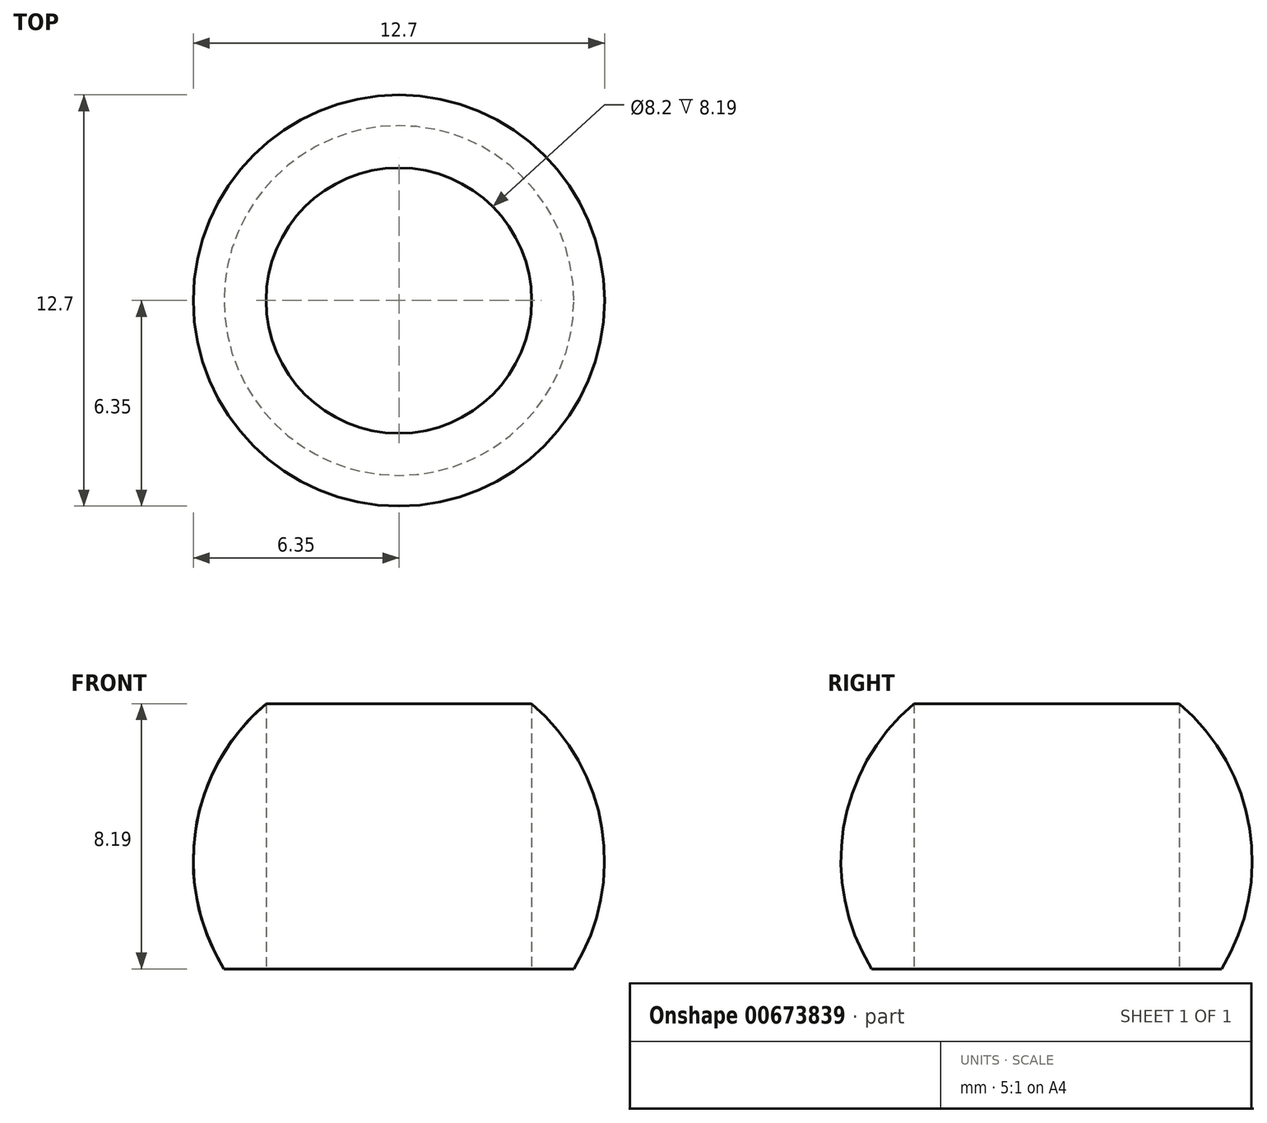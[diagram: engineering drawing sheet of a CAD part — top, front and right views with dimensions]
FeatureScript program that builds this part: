
annotation { "Feature Type Name" : "Feature", "Feature Type Description" : "" }
export const myFeature = defineFeature(function(context is Context, id is Id, definition is map)
    precondition{}
    {
        {
            var Q0;
            Q0=qCreatedBy(makeId("Right.planeOp"),FACE);
            var sketch = newSketch(context, id + "F0", { "sketchPlane" : qUnion([Q0])});
            skLineSegment(sketch, "E0", {"start": v(0, 0) * mm, "end": v(5.4, 0) * mm, "construction": true});
            skArc(sketch, "E1", {"start": v(5.4, 0) * mm, "mid": v(6.27, 4.34) * mm, "end": v(4.1, 8.2) * mm});
            skLineSegment(sketch, "E2", {"start": v(0, 0) * mm, "end": v(0, 9.7) * mm, "construction": true});
            skLineSegment(sketch, "E3", {"start": v(5.4, 0) * mm, "end": v(4.1, 0) * mm});
            skLineSegment(sketch, "E4", {"start": v(4.1, 0) * mm, "end": v(4.1, 8.2) * mm});
            skPoint(sketch, "E5.start.orphan", {"position": v(0, 12) * mm});
            skSolve(sketch);
        }
        {
            var Q0;
            Q0=makeQuery(id+"F0.imprint","IMPRINT",FACE,{"disambiguationData":[TD([[makeQuery(id+"F0.imprint","IMPRINT",EDGE,{"derivedFrom":sQuery(id+"F0.wireOp",EDGE,"E1")}),1.0]])]});
            var Q1;
            Q1=sQuery(id+"F0.wireOp",EDGE,"E2");
            revolve(context, id + "F1", {"entities" : qUnion([Q0]), "axis" : qUnion([Q1]), "revolveType" : RevolveType.FULL});
        }
    });
